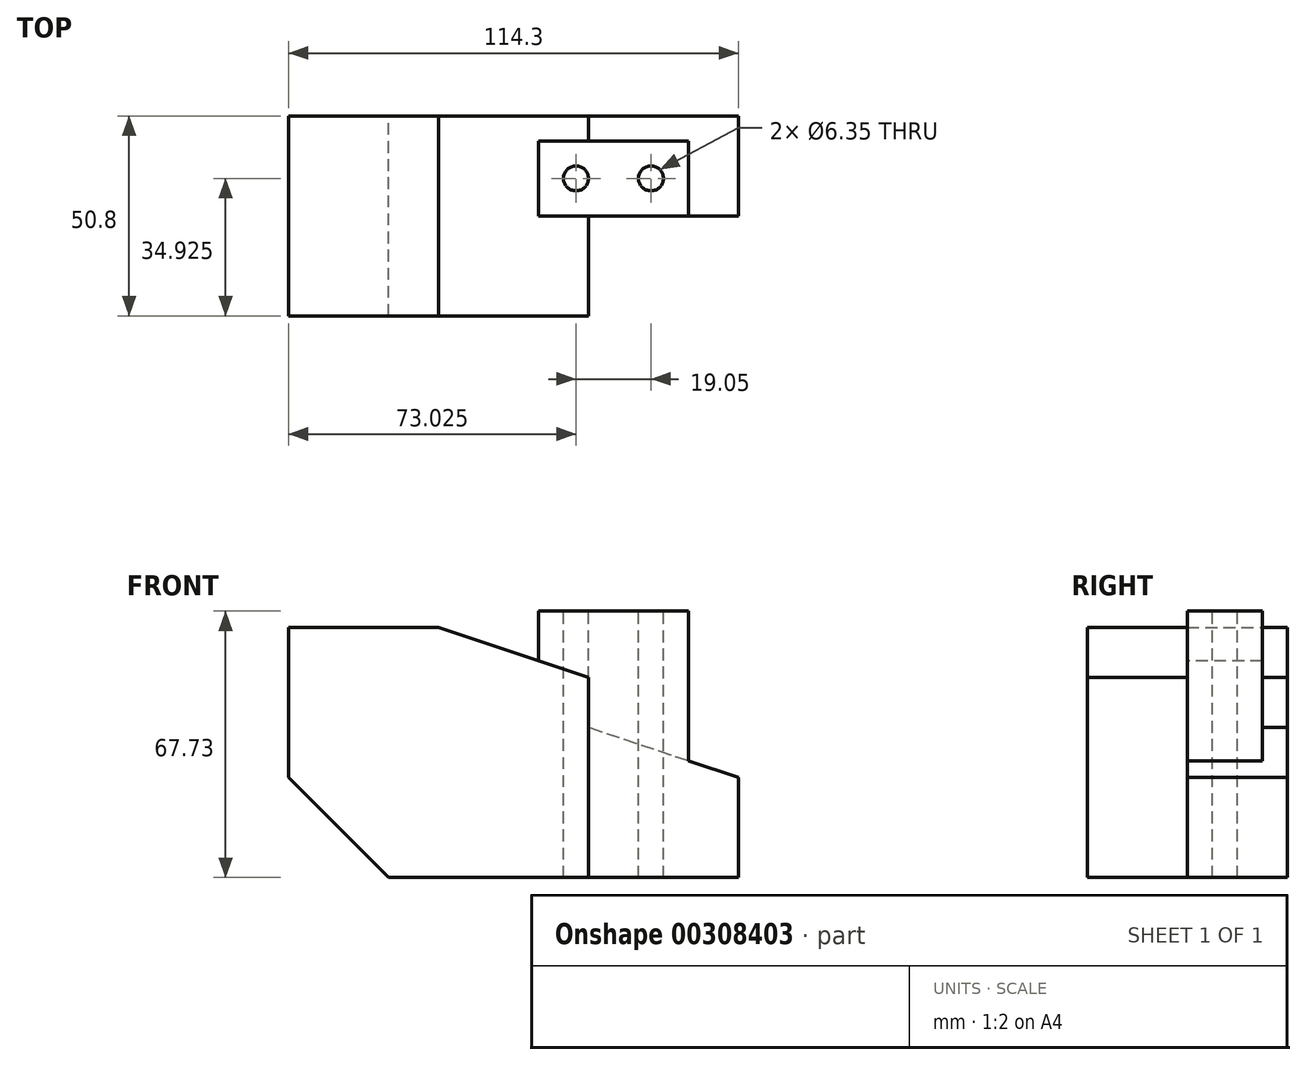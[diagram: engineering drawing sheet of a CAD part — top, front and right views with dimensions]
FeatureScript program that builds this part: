
annotation { "Feature Type Name" : "Feature", "Feature Type Description" : "" }
export const myFeature = defineFeature(function(context is Context, id is Id, definition is map)
    precondition{}
    {
        {
            var Q0;
            Q0=qCreatedBy(makeId("Front.planeOp"),FACE);
            var sketch = newSketch(context, id + "F0", { "sketchPlane" : qUnion([Q0])});
            skLineSegment(sketch, "E0", {"start": v(0, 63.5) * mm, "end": v(0, 25.4) * mm});
            skLineSegment(sketch, "E1", {"start": v(25.4, 0) * mm, "end": v(0, 25.4) * mm});
            skLineSegment(sketch, "E2", {"start": v(25.4, 0) * mm, "end": v(76.2, 0) * mm});
            skLineSegment(sketch, "E3", {"start": v(76.2, 0) * mm, "end": v(76.2, 50.8) * mm});
            skLineSegment(sketch, "E4", {"start": v(76.2, 50.8) * mm, "end": v(38.1, 63.5) * mm});
            skLineSegment(sketch, "E5", {"start": v(38.1, 63.5) * mm, "end": v(0, 63.5) * mm});
            skSolve(sketch);
        }
        {
            var Q0;
            Q0=makeQuery(id+"F0.imprint","IMPRINT",FACE,{"disambiguationData":[TD([[makeQuery(id+"F0.imprint","IMPRINT",EDGE,{"derivedFrom":sQuery(id+"F0.wireOp",EDGE,"E0")}),1.0]])]});
            extrude(context, id + "F1", {"entities" : qUnion([Q0]), "endBound" : BoundingType.SYMMETRIC, "depth" : 50.8 * mm});
        }
        {
            var Q0;
            Q0=qCreatedBy(makeId("Front.planeOp"),FACE);
            var sketch = newSketch(context, id + "F2", { "sketchPlane" : qUnion([Q0])});
            skLineSegment(sketch, "E6", {"start": v(63.5, 55.03) * mm, "end": v(63.5, 67.73) * mm});
            skLineSegment(sketch, "E7", {"start": v(63.5, 67.73) * mm, "end": v(101.6, 67.73) * mm});
            skLineSegment(sketch, "E8", {"start": v(101.6, 67.73) * mm, "end": v(101.6, 29.63) * mm});
            skLineSegment(sketch, "E9", {"start": v(101.6, 29.63) * mm, "end": v(114.3, 25.4) * mm});
            skLineSegment(sketch, "E10", {"start": v(114.3, 25.4) * mm, "end": v(114.3, 0) * mm});
            skLineSegment(sketch, "E11.0", {"start": v(76.2, 50.8) * mm, "end": v(38.1, 63.5) * mm});
            skLineSegment(sketch, "E12.0", {"start": v(76.2, 0) * mm, "end": v(76.2, 50.8) * mm});
            skLineSegment(sketch, "E13", {"start": v(114.3, 0) * mm, "end": v(76.2, 0) * mm});
            skLineSegment(sketch, "E14", {"start": v(76.2, 50.8) * mm, "end": v(63.5, 55.03) * mm});
            skSolve(sketch);
        }
        {
            var Q0;
            Q0=makeQuery(id+"F2.imprint","IMPRINT",FACE,{"disambiguationData":[TD([[makeQuery(id+"F2.imprint","IMPRINT",EDGE,{"derivedFrom":sQuery(id+"F2.wireOp",EDGE,"E6")}),-1.0]])]});
            extrude(context, id + "F3", {"entities" : qUnion([Q0]), "operationType" : NewBodyOperationType.ADD, "oppositeDirection" : true, "depth" : 19.05 * mm});
        }
        {
            var Q0;
            Q0=makeQuery(id+"F3.opExtrude","CAP_FACE",FACE,{"disambiguationData":[OSD([sQuery(id+"F2.wireOp",EDGE,"E6"),sQuery(id+"F2.wireOp",EDGE,"E7"),sQuery(id+"F2.wireOp",EDGE,"E8"),sQuery(id+"F2.wireOp",EDGE,"E9"),sQuery(id+"F2.wireOp",EDGE,"E10"),sQuery(id+"F2.wireOp",EDGE,"E12.0"),sQuery(id+"F2.wireOp",EDGE,"E13"),sQuery(id+"F2.wireOp",EDGE,"E14")])],"isStart":false});
            var sketch = newSketch(context, id + "F4", { "sketchPlane" : qUnion([Q0])});
            skLineSegment(sketch, "E15", {"start": v(-114.3, 25.4) * mm, "end": v(-76.2, 38.1) * mm});
            skLineSegment(sketch, "E16", {"start": v(-76.2, 38.1) * mm, "end": v(-76.2, 0) * mm});
            skLineSegment(sketch, "E17", {"start": v(-76.2, 0) * mm, "end": v(-114.3, 0) * mm});
            skLineSegment(sketch, "E18", {"start": v(-114.3, 0) * mm, "end": v(-114.3, 25.4) * mm});
            skSolve(sketch);
        }
        {
            var Q0;
            {var subQ0=sQuery(id+"F4.wireOp",EDGE,"E16");Q0=makeQuery(id+"F4.imprint","IMPRINT",FACE,{"disambiguationData":[TD([[makeQuery(id+"F4.imprint","IMPRINT",EDGE,{"derivedFrom":subQ0}),1.0]])]});}
            extrude(context, id + "F5", {"entities" : qUnion([Q0]), "operationType" : NewBodyOperationType.ADD, "depth" : 6.35 * mm});
        }
        {
            var Q0;
            Q0=makeQuery(id+"F3.opExtrude","SWEPT_FACE",FACE,{"disambiguationData":[OSD([sQuery(id+"F2.wireOp",EDGE,"E7")])]});
            var sketch = newSketch(context, id + "F6", { "sketchPlane" : qUnion([Q0])});
            skCircle(sketch, "E19", {"center": v(73.03, 9.53) * mm, "radius": 3.18 * mm});
            skCircle(sketch, "E20", {"center": v(92.08, 9.53) * mm, "radius": 3.18 * mm});
            skSolve(sketch);
        }
        {
            var Q0;
            Q0=makeQuery(id+"F6.imprint","IMPRINT",FACE,{"disambiguationData":[TD([[makeQuery(id+"F6.imprint","IMPRINT",EDGE,{"derivedFrom":sQuery(id+"F6.wireOp",EDGE,"E19")}),1.0]])]});
            var Q1;
            Q1=makeQuery(id+"F6.imprint","IMPRINT",FACE,{"disambiguationData":[TD([[makeQuery(id+"F6.imprint","IMPRINT",EDGE,{"derivedFrom":sQuery(id+"F6.wireOp",EDGE,"E20")}),1.0]])]});
            extrude(context, id + "F7", {"entities" : qUnion([Q0, Q1]), "operationType" : NewBodyOperationType.REMOVE, "endBound" : BoundingType.THROUGH_ALL, "oppositeDirection" : true, "depth" : 25.4 * mm});
        }
    });
